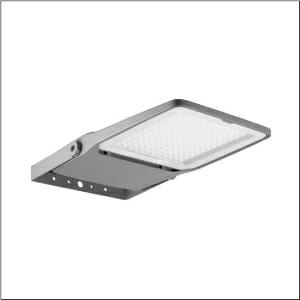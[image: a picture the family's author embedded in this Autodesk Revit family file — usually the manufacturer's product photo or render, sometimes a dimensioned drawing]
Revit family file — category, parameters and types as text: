
# Revit family: floodlight_fl_20_midi___pl61_5xa7682e1c2ac_7ec6
name_source: partatom
category: Lighting Fixtures
units: mm (PartAtom-declared; Revit-internal decimal feet)

## family parameters
Cut with Voids When Loaded = No
Host = Face
Light Source = No
Part Type = Normal
Room Calculation Point = No
Round Connector Dimension = Use Diameter
Shared = No

## types (1)
- --- (1 x LED 3000K / CRI = 80 (unbekannt), 21280 lm, 3000K)
    Apparent Load = 208 VA
    CIE Flux Codes = 33 65 98 100 100
    Color Rendering = 80
    Color Temperature = 3000K
    Default Elevation = 1800 mm
    Description = Floodlight FL 20 midi, floodlight, primary light control with lens, of plastic, primary optical cover: protective disc, of toughened safety glass, transparent, light distribution: PL61, light emission: direct distribution, primary light characteristic: asymmetric, installation type: surface-mounted, LED, High Power LED, rated luminous flux: 21.280lm, luminous efficacy: 102lm/W, light colour: 830, colour temperature: 3000K, control gear: ECG Plus, control: digital communication interface, time-dependent luminous flux control, flexible luminous flux parameterisation, power reduction, overheat protection, electronic power reduction, with terminal, 5-pole, max. 2.5mm², mains connection: 220..240V, AC, 50/60Hz, rated input power: 208W, LED unit, of diecast aluminium, powder-coated, Siteco® metallic grey (DB 702S), corrosivity category C5 mid according to DIN EN ISO 12944, incl. 1x M20 cable gland for cable Ø 6.5..12mm, length: 731mm, width: 450mm, height: 76mm, housing frame, of diecast aluminium, powder-coated, Siteco® metallic grey (DB 702S), wall fastening, of steel, powder-coated, Siteco® metallic grey (DB 702S), DALI, protection rating (complete): IP66, insulation class (complete): insulation class II (safety insulation), certification: CE, ENEC, VDE, protection symbol: D, permissible operating ambient temperature: -40..+40°C, permissible operating ambient temperature for outdoor applications: -40..+50°C, standard: DIN EN 12944, packaging unit: 1 piece

Light Distribution: PL61
    Height = 76 mm
    Lamp = 1 x LED 3000K / CRI >= 80 (unbekannt)
    Lamp Light Flux = 21280 lm
    Lamp count = 1
    Length = 731 mm
    Luminous efficacy = 102 lm/W
    Manufacturer = Siteco
    ModVariant = No
    Model = 5XA7682E1C2AC
    Mounting Place = Wall
    Mounting Type = Surface mounted
    Number of Poles = 1
    OnlyDefault = Yes
    Power Factor = 1
    Product Name = Floodlight FL 20 midi | PL61
    Product group = floodlight | wall mounted
    ProductGroupID = 2001
    Protection Class = Protection class II
    Protection Degree = IP 66
    RLX_Detail_Level = 1
    RLX_Emergency_Light_Flux = 0 lm
    RLX_Emergency_Type = 0
    RLX_Emergency_Type_DB = No
    RlxData = <blob elided: 91945 chars, md5=9dbf80f3>
    Socket = socket
    Standby Power = 0 W
    System Light Flux = 21280 lm
    System Power = 208 W
    Type Comments = factory setting: luminous flux: 100 % | dim-lin: 254 | 484 mA
    Type Image = l_1005944.jpg
    URL = http://relux.com
    VarID = @adj_147027
    Voltage = 0 V
    Weight = 0.00 kg
    Width = 450 mm

## geometry (parser evidence)
native form markers: Blend x4, Sweep x14
no freeform markers — native parametric forms only
